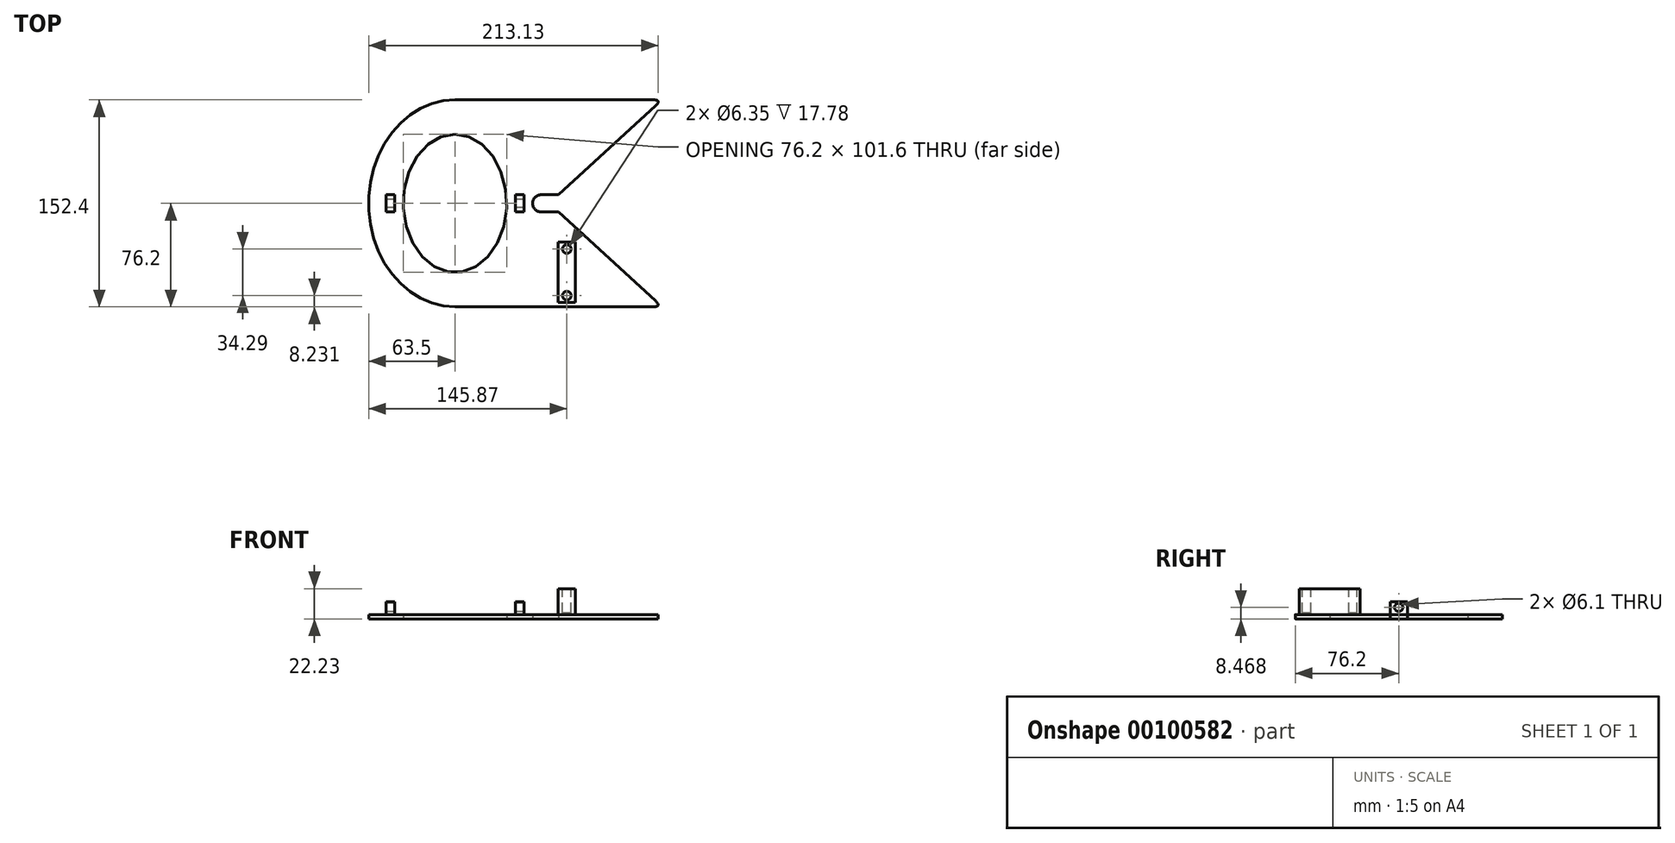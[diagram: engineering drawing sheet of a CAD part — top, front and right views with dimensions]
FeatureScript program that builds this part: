
annotation { "Feature Type Name" : "Feature", "Feature Type Description" : "" }
export const myFeature = defineFeature(function(context is Context, id is Id, definition is map)
    precondition{}
    {
        {
            var Q0;
            Q0=qCreatedBy(makeId("Top.planeOp"),FACE);
            var sketch = newSketch(context, id + "F0", { "sketchPlane" : qUnion([Q0])});
            skLineSegment(sketch, "E0.bottom", {"start": v(-76.2, 76.2) * mm, "end": v(76.2, 76.2) * mm});
            skLineSegment(sketch, "E0.top", {"start": v(-76.2, -76.2) * mm, "end": v(76.2, -76.2) * mm});
            skLineSegment(sketch, "E1", {"start": v(0, 6.35) * mm, "end": v(76.2, 76.2) * mm});
            skLineSegment(sketch, "E2", {"start": v(0, -6.35) * mm, "end": v(76.2, -76.2) * mm});
            skArc(sketch, "E3", {"start": v(-12.7, 6.35) * mm, "mid": v(-19.05, 0) * mm, "end": v(-12.7, -6.35) * mm});
            skLineSegment(sketch, "E4", {"start": v(0, 6.35) * mm, "end": v(-12.7, 6.35) * mm});
            skLineSegment(sketch, "E5", {"start": v(-12.7, -6.35) * mm, "end": v(0, -6.35) * mm});
            skLineSegment(sketch, "E6", {"start": v(-12.7, 6.35) * mm, "end": v(-12.7, -6.35) * mm, "construction": true});
            skPoint(sketch, "E7.centerSnap0", {"position": v(-19.05, 0) * mm});
            skEllipse(sketch, "E8", {"center": v(-76.2, 0) * mm, "majorRadius": 50.8 * mm, "minorRadius": 38.1 * mm, "majorAxis": v(0, 1)});
            skEllipticalArc(sketch, "E9", {});
            skLineSegment(sketch, "E10.bottom", {"start": v(-127, 6.35) * mm, "end": v(-120.65, 6.35) * mm});
            skLineSegment(sketch, "E10.top", {"start": v(-127, -6.35) * mm, "end": v(-120.65, -6.35) * mm});
            skLineSegment(sketch, "E10.left", {"start": v(-127, 6.35) * mm, "end": v(-127, -6.35) * mm});
            skLineSegment(sketch, "E10.right", {"start": v(-120.65, 6.35) * mm, "end": v(-120.65, -6.35) * mm});
            skLineSegment(sketch, "E11.bottom", {"start": v(-31.75, 6.35) * mm, "end": v(-25.4, 6.35) * mm});
            skLineSegment(sketch, "E11.top", {"start": v(-31.75, -6.35) * mm, "end": v(-25.4, -6.35) * mm});
            skLineSegment(sketch, "E11.left", {"start": v(-31.75, 6.35) * mm, "end": v(-31.75, -6.35) * mm});
            skLineSegment(sketch, "E11.right", {"start": v(-25.4, 6.35) * mm, "end": v(-25.4, -6.35) * mm});
            const initialGuessF0  = {"E9": [-0.0762, 0, 0, 1, 0.0762, 0.0635, 0, 3.141592653589793]};
            skSetInitialGuess(sketch, initialGuessF0);
            skSolve(sketch);
        }
        {
            var Q0;
            Q0=makeQuery(id+"F0.imprint","IMPRINT",FACE,{"disambiguationData":[TD([[makeQuery(id+"F0.imprint","IMPRINT",EDGE,{"derivedFrom":sQuery(id+"F0.wireOp",EDGE,"E0.bottom")}),-1.0]])]});
            extrude(context, id + "F1", {"entities" : qUnion([Q0]), "depth" : 3.17 * mm});
        }
        {
            var Q0;
            Q0=makeQuery(id+"F1.opExtrude","SWEPT_EDGE",EDGE,{"disambiguationData":[OSD([sQuery(id+"F0.wireOp",EDGE,"E0.top"),sQuery(id+"F0.wireOp",EDGE,"E2")])]});
            fillet(context, id + "F2", {"entities" : qUnion([Q0]), "radius" : 2.54 * mm, "tangentPropagation" : true, "rho" : 0.5, "crossSection" : FilletCrossSection.CONIC, "allowEdgeOverflow" : false});
        }
        {
            var Q0;
            Q0=makeQuery(id+"F1.opExtrude","SWEPT_EDGE",EDGE,{"disambiguationData":[OSD([sQuery(id+"F0.wireOp",EDGE,"E0.bottom"),sQuery(id+"F0.wireOp",EDGE,"E1")])]});
            fillet(context, id + "F3", {"entities" : qUnion([Q0]), "radius" : 2.54 * mm, "tangentPropagation" : true, "rho" : 0.5, "crossSection" : FilletCrossSection.CONIC, "allowEdgeOverflow" : false});
        }
        {
            var Q0;
            Q0=makeQuery(id+"F0.imprint","IMPRINT",FACE,{"disambiguationData":[TD([[makeQuery(id+"F0.imprint","IMPRINT",EDGE,{"derivedFrom":sQuery(id+"F0.wireOp",EDGE,"E11.bottom")}),-1.0]])]});
            var Q1;
            Q1=makeQuery(id+"F0.imprint","IMPRINT",FACE,{"disambiguationData":[TD([[makeQuery(id+"F0.imprint","IMPRINT",EDGE,{"derivedFrom":sQuery(id+"F0.wireOp",EDGE,"E10.bottom")}),-1.0]])]});
            extrude(context, id + "F4", {"entities" : qUnion([Q0, Q1]), "operationType" : NewBodyOperationType.ADD, "depth" : 12.7 * mm});
        }
        {
            var Q0;
            Q0=makeQuery(id+"F4.opExtrude","SWEPT_FACE",FACE,{"disambiguationData":[OSD([sQuery(id+"F0.wireOp",EDGE,"E10.left")])]});
            var sketch = newSketch(context, id + "F5", { "sketchPlane" : qUnion([Q0])});
            skPoint(sketch, "E12", {"position": v(0, 8.47) * mm});
            skSolve(sketch);
        }
        {
            var Q0;
            Q0=sQuery(id+"F5.wireOp",VERTEX,"E12");
            var Q1;
            Q1=makeQuery(id+"F1.opExtrude","SWEPT_BODY",BODY,{"disambiguationData":[OSD([sQuery(id+"F0.wireOp",EDGE,"E0.bottom"),sQuery(id+"F0.wireOp",EDGE,"E0.top"),sQuery(id+"F0.wireOp",EDGE,"E1"),sQuery(id+"F0.wireOp",EDGE,"E2"),sQuery(id+"F0.wireOp",EDGE,"E3"),sQuery(id+"F0.wireOp",EDGE,"E4"),sQuery(id+"F0.wireOp",EDGE,"E5"),sQuery(id+"F0.wireOp",EDGE,"E8"),sQuery(id+"F0.wireOp",EDGE,"E9"),sQuery(id+"F0.wireOp",EDGE,"E10.bottom"),sQuery(id+"F0.wireOp",EDGE,"E10.top"),sQuery(id+"F0.wireOp",EDGE,"E10.left"),sQuery(id+"F0.wireOp",EDGE,"E10.right"),sQuery(id+"F0.wireOp",EDGE,"E11.bottom"),sQuery(id+"F0.wireOp",EDGE,"E11.top"),sQuery(id+"F0.wireOp",EDGE,"E11.left"),sQuery(id+"F0.wireOp",EDGE,"E11.right")])]});
            hole(context, id + "F6", {"style" : HoleStyle.SIMPLE, "endStyle" : HoleEndStyle.THROUGH, "holeDiameter" : 6.1 * mm, "locations" : qUnion([Q0]), "scope" : qUnion([Q1]), "isTappedThrough" : true});
        }
        {
            var Q0;
            Q0=makeQuery(id+"F1.opExtrude","CAP_FACE",FACE,{"disambiguationData":[OSD([sQuery(id+"F0.wireOp",EDGE,"E0.bottom"),sQuery(id+"F0.wireOp",EDGE,"E0.top"),sQuery(id+"F0.wireOp",EDGE,"E1"),sQuery(id+"F0.wireOp",EDGE,"E2"),sQuery(id+"F0.wireOp",EDGE,"E3"),sQuery(id+"F0.wireOp",EDGE,"E4"),sQuery(id+"F0.wireOp",EDGE,"E5"),sQuery(id+"F0.wireOp",EDGE,"E8"),sQuery(id+"F0.wireOp",EDGE,"E9"),sQuery(id+"F0.wireOp",EDGE,"E10.bottom"),sQuery(id+"F0.wireOp",EDGE,"E10.top"),sQuery(id+"F0.wireOp",EDGE,"E10.left"),sQuery(id+"F0.wireOp",EDGE,"E10.right"),sQuery(id+"F0.wireOp",EDGE,"E11.bottom"),sQuery(id+"F0.wireOp",EDGE,"E11.top"),sQuery(id+"F0.wireOp",EDGE,"E11.left"),sQuery(id+"F0.wireOp",EDGE,"E11.right")])],"isStart":false});
            var sketch = newSketch(context, id + "F7", { "sketchPlane" : qUnion([Q0])});
            skLineSegment(sketch, "E13.bottom", {"start": v(12.52, -73.05) * mm, "end": v(-0.18, -73.05) * mm});
            skLineSegment(sketch, "E13.top", {"start": v(12.52, -28.6) * mm, "end": v(-0.18, -28.6) * mm});
            skLineSegment(sketch, "E13.left", {"start": v(12.52, -73.05) * mm, "end": v(12.52, -28.6) * mm});
            skLineSegment(sketch, "E13.right", {"start": v(-0.18, -73.05) * mm, "end": v(-0.18, -28.6) * mm});
            skSolve(sketch);
        }
        {
            var Q0;
            Q0=makeQuery(id+"F7.imprint","IMPRINT",FACE,{"disambiguationData":[TD([[makeQuery(id+"F7.imprint","IMPRINT",EDGE,{"derivedFrom":sQuery(id+"F7.wireOp",EDGE,"E13.bottom")}),-1.0]])]});
            extrude(context, id + "F8", {"entities" : qUnion([Q0]), "operationType" : NewBodyOperationType.ADD, "depth" : 19.05 * mm});
        }
        {
            var Q0;
            Q0=makeQuery(id+"F8.opExtrude","CAP_FACE",FACE,{"disambiguationData":[OSD([sQuery(id+"F7.wireOp",EDGE,"E13.bottom"),sQuery(id+"F7.wireOp",EDGE,"E13.top"),sQuery(id+"F7.wireOp",EDGE,"E13.left"),sQuery(id+"F7.wireOp",EDGE,"E13.right")])],"isStart":false});
            var sketch = newSketch(context, id + "F9", { "sketchPlane" : qUnion([Q0])});
            skCircle(sketch, "E14", {"center": v(6.17, -67.97) * mm, "radius": 3.18 * mm});
            skPoint(sketch, "E14.centerSnap0", {"position": v(6.17, -73.05) * mm});
            skPoint(sketch, "E14.centerSnap1", {"position": v(12.52, -67.97) * mm});
            skCircle(sketch, "E15", {"center": v(6.17, -33.68) * mm, "radius": 3.18 * mm});
            skSolve(sketch);
        }
        {
            var Q0;
            Q0=makeQuery(id+"F9.imprint","IMPRINT",FACE,{"disambiguationData":[TD([[makeQuery(id+"F9.imprint","IMPRINT",EDGE,{"derivedFrom":sQuery(id+"F9.wireOp",EDGE,"E14")}),1.0]])]});
            extrude(context, id + "F10", {"entities" : qUnion([Q0]), "operationType" : NewBodyOperationType.REMOVE, "oppositeDirection" : true, "depth" : 17.78 * mm});
        }
        {
            var Q0;
            Q0 = qSketchRegion(id + "F9", true);
            extrude(context, id + "F11", {"entities" : qUnion([Q0]), "operationType" : NewBodyOperationType.REMOVE, "oppositeDirection" : true, "depth" : 17.78 * mm});
        }
    });
